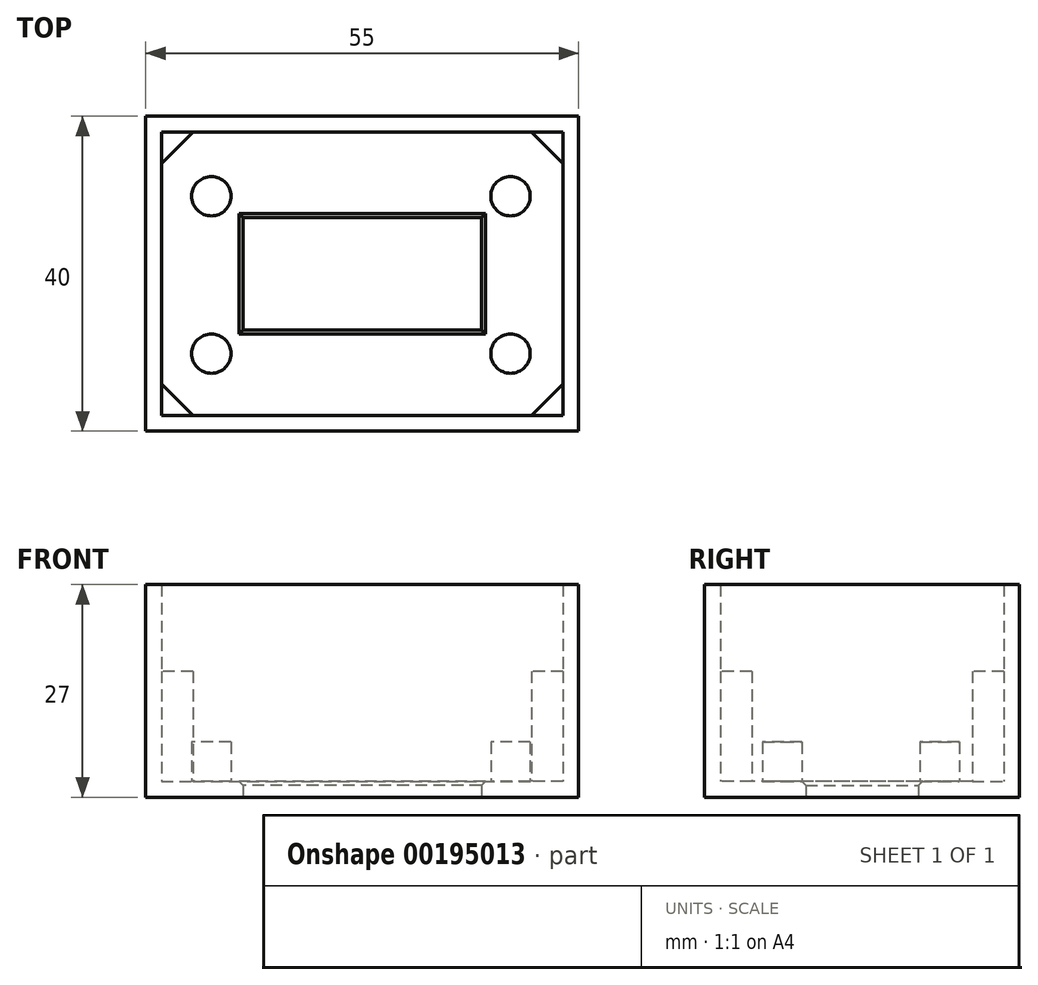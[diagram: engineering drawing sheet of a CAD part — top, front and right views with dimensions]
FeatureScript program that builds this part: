
annotation { "Feature Type Name" : "Feature", "Feature Type Description" : "" }
export const myFeature = defineFeature(function(context is Context, id is Id, definition is map)
    precondition{}
    {
        {
            var Q0;
            Q0=qCreatedBy(makeId("Top.planeOp"),FACE);
            var sketch = newSketch(context, id + "F0", { "sketchPlane" : qUnion([Q0])});
            skLineSegment(sketch, "E0.bottom", {"start": v(-27.5, 20) * mm, "end": v(27.5, 20) * mm});
            skLineSegment(sketch, "E0.top", {"start": v(-27.5, -20) * mm, "end": v(27.5, -20) * mm});
            skLineSegment(sketch, "E0.left", {"start": v(-27.5, 20) * mm, "end": v(-27.5, -20) * mm});
            skLineSegment(sketch, "E0.right", {"start": v(27.5, 20) * mm, "end": v(27.5, -20) * mm});
            skPoint(sketch, "E0.middle", {"position": v(0, 0) * mm});
            skLineSegment(sketch, "E1.bottom", {"start": v(-25.5, 18) * mm, "end": v(25.5, 18) * mm});
            skLineSegment(sketch, "E1.top", {"start": v(-25.5, -18) * mm, "end": v(25.5, -18) * mm});
            skLineSegment(sketch, "E1.left", {"start": v(-25.5, 18) * mm, "end": v(-25.5, -18) * mm});
            skLineSegment(sketch, "E1.right", {"start": v(25.5, 18) * mm, "end": v(25.5, -18) * mm});
            skSolve(sketch);
        }
        {
            var Q0;
            Q0=makeQuery(id+"F0.imprint","IMPRINT",FACE,{"disambiguationData":[TD([[makeQuery(id+"F0.imprint","IMPRINT",EDGE,{"derivedFrom":sQuery(id+"F0.wireOp",EDGE,"E0.bottom")}),-1.0]])]});
            var sketch = newSketch(context, id + "F1", { "sketchPlane" : qUnion([Q0])});
            skLineSegment(sketch, "E2.bottom", {"start": v(15.15, 7.15) * mm, "end": v(-15.15, 7.15) * mm});
            skLineSegment(sketch, "E2.top", {"start": v(15.15, -7.15) * mm, "end": v(-15.15, -7.15) * mm});
            skLineSegment(sketch, "E2.left", {"start": v(15.15, 7.15) * mm, "end": v(15.15, -7.15) * mm});
            skLineSegment(sketch, "E2.right", {"start": v(-15.15, 7.15) * mm, "end": v(-15.15, -7.15) * mm});
            skPoint(sketch, "E2.middle", {"position": v(0, 0) * mm});
            skSolve(sketch);
        }
        {
            var Q0;
            Q0=makeQuery(id+"F1.imprint","IMPRINT",FACE,{"disambiguationData":[TD([[makeQuery(id+"F1.imprint","IMPRINT",EDGE,{"derivedFrom":sQuery(id+"F1.wireOp",EDGE,"E2.bottom")}),-1.0]])]});
            extrude(context, id + "F2", {"entities" : qUnion([Q0]), "depth" : 2 * mm});
        }
        {
            var Q0;
            Q0=makeQuery(id+"F2.opExtrude","CAP_FACE",FACE,{"disambiguationData":[OSD([sQuery(id+"F0.wireOp",EDGE,"E1.bottom"),sQuery(id+"F0.wireOp",EDGE,"E1.top"),sQuery(id+"F0.wireOp",EDGE,"E1.left"),sQuery(id+"F0.wireOp",EDGE,"E1.right"),sQuery(id+"F1.wireOp",EDGE,"E2.bottom"),sQuery(id+"F1.wireOp",EDGE,"E2.top"),sQuery(id+"F1.wireOp",EDGE,"E2.left"),sQuery(id+"F1.wireOp",EDGE,"E2.right")])],"isStart":false});
            var sketch = newSketch(context, id + "F3", { "sketchPlane" : qUnion([Q0])});
            skCircle(sketch, "E3", {"center": v(-19.15, 9.85) * mm, "radius": 2.5 * mm});
            skCircle(sketch, "E4", {"center": v(-19.15, -10.15) * mm, "radius": 2.5 * mm});
            skCircle(sketch, "E5", {"center": v(18.85, -10.15) * mm, "radius": 2.5 * mm});
            skCircle(sketch, "E6", {"center": v(18.85, 9.85) * mm, "radius": 2.5 * mm});
            skLineSegment(sketch, "E7", {"start": v(-25.5, 18) * mm, "end": v(-21.5, 18) * mm});
            skLineSegment(sketch, "E8", {"start": v(-21.5, 18) * mm, "end": v(-25.5, 14) * mm});
            skLineSegment(sketch, "E9", {"start": v(-25.5, 14) * mm, "end": v(-25.5, 18) * mm});
            skLineSegment(sketch, "E10", {"start": v(25.5, 18) * mm, "end": v(25.5, 14) * mm});
            skLineSegment(sketch, "E11", {"start": v(25.5, 14) * mm, "end": v(21.5, 18) * mm});
            skLineSegment(sketch, "E12", {"start": v(21.5, 18) * mm, "end": v(25.5, 18) * mm});
            skLineSegment(sketch, "E13", {"start": v(25.5, -18) * mm, "end": v(25.5, -14) * mm});
            skLineSegment(sketch, "E14", {"start": v(25.5, -14) * mm, "end": v(21.5, -18) * mm});
            skLineSegment(sketch, "E15", {"start": v(21.5, -18) * mm, "end": v(25.5, -18) * mm});
            skLineSegment(sketch, "E16", {"start": v(-25.5, -18) * mm, "end": v(-25.5, -14) * mm});
            skLineSegment(sketch, "E17", {"start": v(-25.5, -14) * mm, "end": v(-21.5, -18) * mm});
            skLineSegment(sketch, "E18", {"start": v(-21.5, -18) * mm, "end": v(-25.5, -18) * mm});
            skSolve(sketch);
        }
        {
            var Q0;
            Q0=makeQuery(id+"F3.imprint","IMPRINT",FACE,{"disambiguationData":[TD([[makeQuery(id+"F3.imprint","IMPRINT",EDGE,{"derivedFrom":sQuery(id+"F3.wireOp",EDGE,"E3")}),1.0]])]});
            var Q1;
            Q1=makeQuery(id+"F3.imprint","IMPRINT",FACE,{"disambiguationData":[TD([[makeQuery(id+"F3.imprint","IMPRINT",EDGE,{"derivedFrom":sQuery(id+"F3.wireOp",EDGE,"E6")}),1.0]])]});
            var Q2;
            Q2=makeQuery(id+"F3.imprint","IMPRINT",FACE,{"disambiguationData":[TD([[makeQuery(id+"F3.imprint","IMPRINT",EDGE,{"derivedFrom":sQuery(id+"F3.wireOp",EDGE,"E5")}),1.0]])]});
            var Q3;
            Q3=makeQuery(id+"F3.imprint","IMPRINT",FACE,{"disambiguationData":[TD([[makeQuery(id+"F3.imprint","IMPRINT",EDGE,{"derivedFrom":sQuery(id+"F3.wireOp",EDGE,"E4")}),1.0]])]});
            extrude(context, id + "F4", {"entities" : qUnion([Q0, Q1, Q2, Q3]), "operationType" : NewBodyOperationType.ADD, "depth" : 5 * mm});
        }
        {
            var Q0;
            Q0=makeQuery(id+"F3.imprint","IMPRINT",FACE,{"disambiguationData":[TD([[makeQuery(id+"F3.imprint","IMPRINT",EDGE,{"derivedFrom":sQuery(id+"F3.wireOp",EDGE,"E7")}),-1.0]])]});
            var Q1;
            Q1=makeQuery(id+"F3.imprint","IMPRINT",FACE,{"disambiguationData":[TD([[makeQuery(id+"F3.imprint","IMPRINT",EDGE,{"derivedFrom":sQuery(id+"F3.wireOp",EDGE,"E16")}),1.0]])]});
            var Q2;
            Q2=makeQuery(id+"F3.imprint","IMPRINT",FACE,{"disambiguationData":[TD([[makeQuery(id+"F3.imprint","IMPRINT",EDGE,{"derivedFrom":sQuery(id+"F3.wireOp",EDGE,"E13")}),-1.0]])]});
            var Q3;
            Q3=makeQuery(id+"F3.imprint","IMPRINT",FACE,{"disambiguationData":[TD([[makeQuery(id+"F3.imprint","IMPRINT",EDGE,{"derivedFrom":sQuery(id+"F3.wireOp",EDGE,"E10")}),-1.0]])]});
            extrude(context, id + "F5", {"entities" : qUnion([Q0, Q1, Q2, Q3]), "operationType" : NewBodyOperationType.ADD, "depth" : 14 * mm});
        }
        {
            var Q0;
            Q0=makeQuery(id+"F0.imprint","IMPRINT",FACE,{"disambiguationData":[TD([[makeQuery(id+"F0.imprint","IMPRINT",EDGE,{"derivedFrom":sQuery(id+"F0.wireOp",EDGE,"E0.bottom")}),-1.0]])]});
            extrude(context, id + "F6", {"entities" : qUnion([Q0]), "operationType" : NewBodyOperationType.ADD, "depth" : 27 * mm});
        }
        {
            var Q0;
            Q0=makeQuery(id+"F2.opExtrude","CAP_EDGE",EDGE,{"disambiguationData":[OSD([sQuery(id+"F1.wireOp",EDGE,"E2.bottom")])],"isStart":false});
            var Q1;
            Q1=makeQuery(id+"F2.opExtrude","CAP_EDGE",EDGE,{"disambiguationData":[OSD([sQuery(id+"F1.wireOp",EDGE,"E2.left")])],"isStart":false});
            var Q2;
            Q2=makeQuery(id+"F2.opExtrude","CAP_EDGE",EDGE,{"disambiguationData":[OSD([sQuery(id+"F1.wireOp",EDGE,"E2.top")])],"isStart":false});
            var Q3;
            Q3=makeQuery(id+"F2.opExtrude","CAP_EDGE",EDGE,{"disambiguationData":[OSD([sQuery(id+"F1.wireOp",EDGE,"E2.right")])],"isStart":false});
            chamfer(context, id + "F7", {"entities" : qUnion([Q0, Q1, Q2, Q3]), "width" : .5 * mm, "tangentPropagation" : true});
        }
    });
